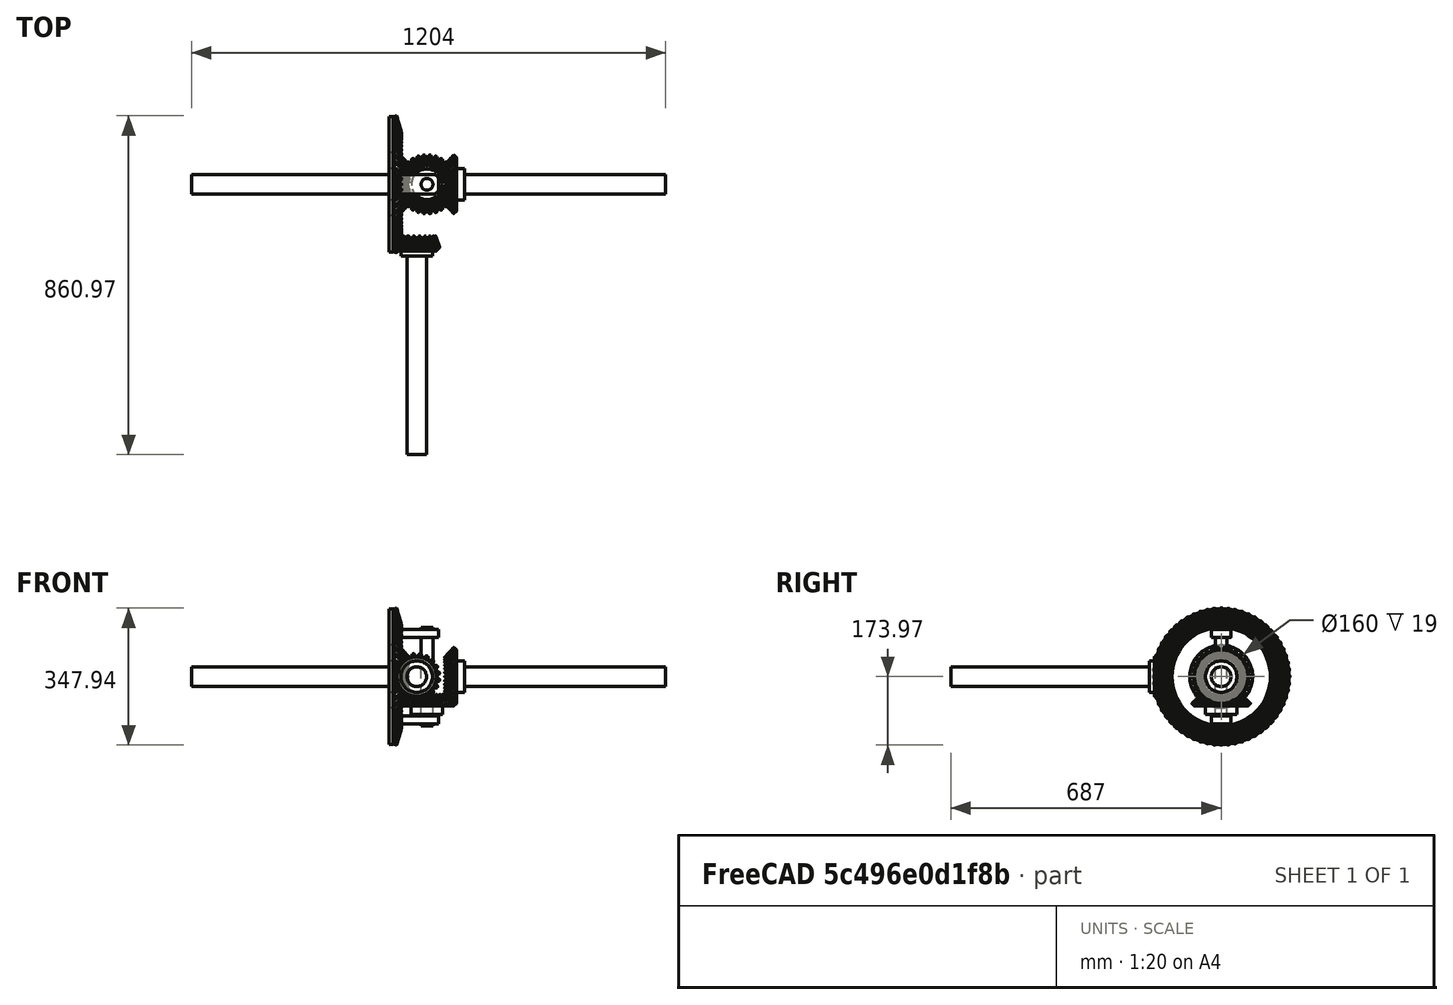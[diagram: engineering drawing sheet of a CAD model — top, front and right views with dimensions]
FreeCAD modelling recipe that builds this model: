
FCSTD DOCUMENT  (FreeCAD 0.18R13524 (Git))
Label: DIFERENCIAL- CJ
License: All rights reserved
LicenseURL: http://en.wikipedia.org/wiki/All_rights_reserved
objects: Part::FeaturePython×7, Part::Cylinder×4, Part::MultiFuse×4, Part::Box×1, Part::Fillet×1
note: 17 computed .brp shape members not serialized (recipe doc carries the construction recipe); baked Part::Feature solids carry a one-line shape summary decoded from their .brp

FEATURE [Part::FeaturePython] DIFERENCIAL_3_01  # a2plus imported part (geometry in sourceFile) (typed FeaturePython)
  Placement = pos=(0,0,0) rot=(0,0,1;0.314159rad)
  fixedPosition = true
  sourceFile = <userpath>/RSRV/FREECAD/50-DIFERENCIAL/DIFERENCIAL-3.FCStd
  timeLastImport = 1.52694e+09
  updateColors = true
FEATURE [Part::FeaturePython] DIFERENCIAL_3_01001  # a2plus imported part (geometry in sourceFile) (typed FeaturePython)
  Placement = pos=(0,0,0) rot=(0,-1,0;1.5708rad)
  fixedPosition = false
  sourceFile = <userpath>/RSRV/FREECAD/50-DIFERENCIAL/DIFERENCIAL-3.FCStd
  timeLastImport = 1.52694e+09
  updateColors = true
FEATURE [Part::FeaturePython] Clone  label="DIFERENCIAL_3_01002"  # Draft clone (typed FeaturePython)
  AttacherType = Attacher::AttachEngine3D
  Fuse = false
  Objects = -> [DIFERENCIAL_3_01]
  Placement = pos=(0,0,0) rot=(-0.156434,0.987688,0;3.14159rad)
  Scale = (1,1,1)
FEATURE [Part::FeaturePython] Clone001  label="DIFERENCIAL_3_01003"  # Draft clone (typed FeaturePython)
  AttacherType = Attacher::AttachEngine3D
  Fuse = false
  Objects = -> [DIFERENCIAL_3_01001]
  Placement = pos=(0,0,0) rot=(0.707107,0,0.707107;3.14159rad)
  Scale = (1,1,1)
FEATURE [Part::FeaturePython] DIFERENCIAL_1_01  # a2plus imported part (geometry in sourceFile) (typed FeaturePython)
  Placement = pos=(-25,0,0) rot=(0,-1,0;1.5708rad)
  fixedPosition = false
  sourceFile = <userpath>/RSRV/FREECAD/50-DIFERENCIAL/DIFERENCIAL-1.FCStd
  timeLastImport = 1.52693e+09
  updateColors = true
FEATURE [Part::FeaturePython] DIFERENCIAL_2_01  # a2plus imported part (geometry in sourceFile) (typed FeaturePython)
  Placement = pos=(-26,0,0) rot=(0.862856,0.357407,-0.357407;1.71777rad)
  fixedPosition = false
  sourceFile = <userpath>/RSRV/FREECAD/50-DIFERENCIAL/DIFERENCIAL-2.FCStd
  timeLastImport = 1.52693e+09
  updateColors = true
FEATURE [Part::Cylinder] Cylinder  label="Cilindro"
  Angle = 360
  AttacherType = Attacher::AttachEngine3D
  Height = 250
  Placement = pos=(0,0,-125) rot=(0,0,1;0rad)
  Radius = 15
FEATURE [Part::Box] Box  label="Cubo"
  AttacherType = Attacher::AttachEngine3D
  Height = 20
  Length = 110
  Placement = pos=(-80,-25,100) rot=(0,0,1;0rad)
  Width = 50
FEATURE [Part::Fillet] Fillet
  Base = -> Box
  Edges = 2 edges r=15: [Edge5,Edge7]
FEATURE [Part::FeaturePython] Clone002  label="Fillet001"  # Draft clone (typed FeaturePython)
  AttacherType = Attacher::AttachEngine3D
  Fuse = false
  Objects = -> [Fillet]
  Placement = pos=(0,0,-220) rot=(0,0,1;0rad)
  Scale = (1,1,1)
FEATURE [Part::Cylinder] Cylinder001  label="Cilindro001"
  Angle = 360
  AttacherType = Attacher::AttachEngine3D
  Height = 510
  Placement = pos=(96,0,0) rot=(0,1,0;1.5708rad)
  Radius = 25
FEATURE [Part::Cylinder] Cylinder002  label="Cilindro002"
  Angle = 360
  AttacherType = Attacher::AttachEngine3D
  Height = 510
  Placement = pos=(-598,0,0) rot=(0,1,0;1.5708rad)
  Radius = 25
FEATURE [Part::Cylinder] Cylinder003  label="Cilindro003"
  Angle = 360
  AttacherType = Attacher::AttachEngine3D
  Height = 510
  Placement = pos=(-26,-177,0) rot=(1,0,0;1.5708rad)
  Radius = 25
FEATURE [Part::MultiFuse] Fusion
  Shapes = -> [Cylinder003,DIFERENCIAL_2_01]
FEATURE [Part::MultiFuse] Fusion001
  Shapes = -> [Clone002,Fillet,Cylinder,DIFERENCIAL_1_01]
FEATURE [Part::MultiFuse] Fusion002
  Shapes = -> [Cylinder002,DIFERENCIAL_3_01001]
FEATURE [Part::MultiFuse] Fusion003
  Shapes = -> [Clone001,Cylinder001]
